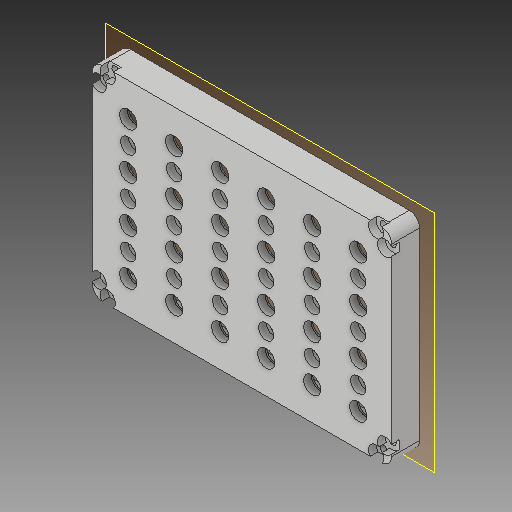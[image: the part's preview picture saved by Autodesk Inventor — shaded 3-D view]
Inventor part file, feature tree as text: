
AUTODESK INVENTOR PART (.ipt)
format: ipt  version: 2019.4 (Build 234330000, 330)  size: 536,064 bytes
history: native  units: mm
features: other x7, sketch x6, reference x6, extrude x4, projected_geometry x3, plane x2, pattern_linear x2, hole x2, shell x1
ambient origin geometry x8: Origin, YZ Plane, XZ Plane, XY Plane, X Axis, Y Axis, Z Axis, Center Point
bodies: Solid1 (feature_tree)
feature tree (33):
  plane  "Work Plane1"
  sketch  "Sketch1"  dims[d0=10.0mm d1=0.0mm d2=4.0mm d3=0.0mm]
  plane  "Work Plane2"
  extrude  "Extrusion1"  Depth=4.0mm TaperAngle=0.0deg
  extrude  "Extrusion2"  Depth=4.0mm TaperAngle=0.0deg
  extrude  "Extrusion3"  Depth=1.0mm
  extrude  "Extrusion4"  Depth=1.0mm
  pattern_linear  "Rectangular Pattern1"  Count1=6 Spacing1=18.0mm
  hole  "Hole1"  [1 undecoded]
  hole  "Hole2"  [1 undecoded]
  pattern_linear  "Rectangular Pattern2"  [2 undecoded]
  shell  "Shell1"  [1 undecoded]
  reference  "Reference1"
  sketch  "Sketch2"  dims[d4=6.75mm d5=4.0mm d6=0.0mm]
  projected_geometry  "Projected Loop1"
  sketch  "Sketch3"  dims[d7=1.0mm d8=0.0mm d9=60.0mm d11=18.0mm]
  reference  "Reference2"
  reference  "Reference3"
  sketch  "Sketch4"  dims[d12=40.0mm d14=18.0mm]
  reference  "Reference4"
  sketch  "Sketch5"  dims[d15=2.8mm d16=6.0mm d17=6.0mm d18=3.0mm d19=90.0deg d20=12.0mm d21=20.594885mm]
  projected_geometry  "Projected Loop2"
  sketch  "Sketch6"  dims[d22=3.0mm d23=6.0mm d24=6.0mm d25=3.0mm d26=90.0deg d27=12.0mm d28=20.594885mm d29=30.0mm d31=18.0mm d32=60.0mm d34=18.0mm d35=1.0mm]
  projected_geometry  "Projected Loop3"
  reference  "Reference5"
  reference  "Reference6"
  other  "Full_HITscope_v0.iam"
  other  "05_Omniscope_base_v1:1"
  other  "00_OV_lens:3"
  other  "Assembly_Omniscope_v1:11"
  other  "01_Camera_Module_left_v0:1"
  other  "00_OV_lens:1"
  other  "Assembly_Omniscope_v1:12"
note: 5 required parameter values undecoded (feature->parameter linkage not recoverable at this tier; creation-order binding heuristic only, values carry confidence <= 0.55)
